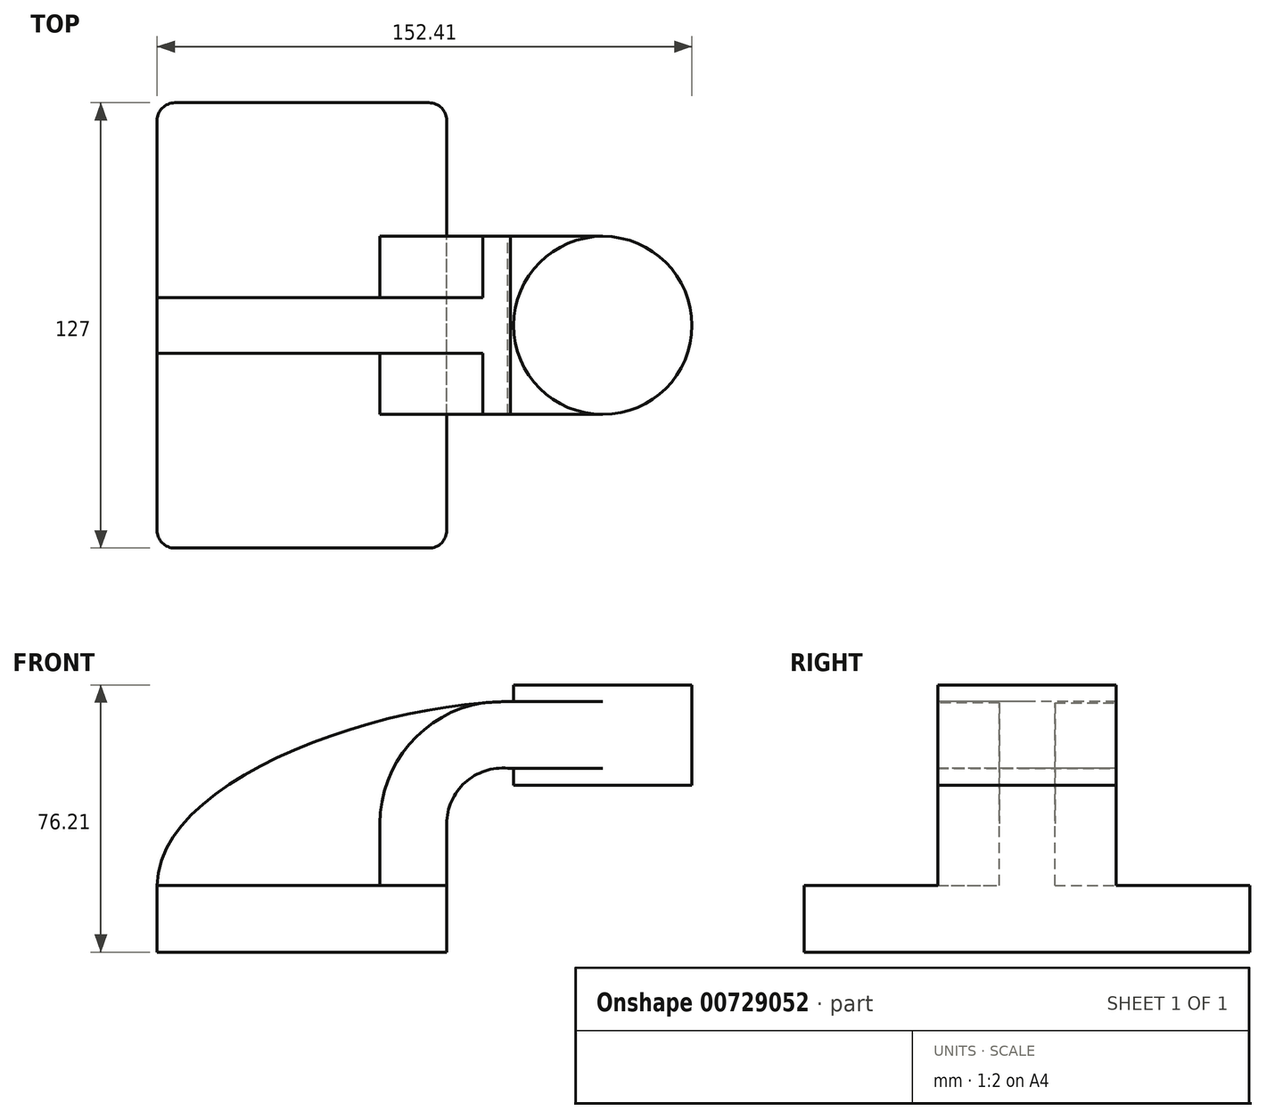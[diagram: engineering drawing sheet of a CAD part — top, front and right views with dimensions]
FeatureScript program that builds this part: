
annotation { "Feature Type Name" : "Feature", "Feature Type Description" : "" }
export const myFeature = defineFeature(function(context is Context, id is Id, definition is map)
    precondition{}
    {
        {
            var Q0;
            Q0=qCreatedBy(makeId("Front.planeOp"),FACE);
            var sketch = newSketch(context, id + "F0", { "sketchPlane" : qUnion([Q0])});
            skLineSegment(sketch, "E0.bottom", {"start": v(41.28, -9.52) * mm, "end": v(-41.28, -9.53) * mm});
            skLineSegment(sketch, "E0.top", {"start": v(41.28, 9.53) * mm, "end": v(-41.28, 9.53) * mm});
            skLineSegment(sketch, "E0.left", {"start": v(41.28, -9.52) * mm, "end": v(41.28, 9.53) * mm});
            skLineSegment(sketch, "E0.right", {"start": v(-41.28, -9.52) * mm, "end": v(-41.28, 9.53) * mm});
            skPoint(sketch, "E0.middle", {"position": v(0, 0) * mm});
            skLineSegment(sketch, "E1.bottom", {"start": v(111.12, 38.1) * mm, "end": v(60.32, 38.1) * mm});
            skLineSegment(sketch, "E1.top", {"start": v(111.12, 66.68) * mm, "end": v(60.32, 66.68) * mm});
            skLineSegment(sketch, "E1.left", {"start": v(111.12, 38.1) * mm, "end": v(111.12, 66.68) * mm});
            skLineSegment(sketch, "E1.right", {"start": v(60.32, 38.1) * mm, "end": v(60.32, 66.67) * mm});
            skPoint(sketch, "E1.middle", {"position": v(85.72, 52.39) * mm});
            skLineSegment(sketch, "E2", {"start": v(41.28, 9.53) * mm, "end": v(41.28, 27.07) * mm});
            skArc(sketch, "E3", {"start": v(41.27, 27.07) * mm, "mid": v(46.47, 38.82) * mm, "end": v(58.66, 42.88) * mm});
            skLineSegment(sketch, "E4", {"start": v(58.66, 42.88) * mm, "end": v(85.9, 42.88) * mm});
            skLineSegment(sketch, "E5.0", {"start": v(59.39, 61.93) * mm, "end": v(85.9, 61.93) * mm});
            skArc(sketch, "E5.1", {"start": v(22.23, 27.07) * mm, "mid": v(33.26, 52.55) * mm, "end": v(59.39, 61.93) * mm});
            skLineSegment(sketch, "E5.2", {"start": v(22.22, 9.53) * mm, "end": v(22.22, 27.07) * mm});
            skLineSegment(sketch, "E6", {"start": v(85.72, 38.1) * mm, "end": v(85.72, 66.68) * mm});
            skFitSpline(sketch, "E7", {"points": [v(-41.28, 9.52) * mm, v(59.39, 61.93) * mm], "startDerivative": vector(0.2, 88.51) * mm, "endDerivative": vector(118.13, 1.81) * mm});
            skSolve(sketch);
        }
        {
            var Q0;
            Q0=makeQuery(id+"F0.imprint","IMPRINT",FACE,{"disambiguationData":[TD([[makeQuery(id+"F0.imprint","IMPRINT",EDGE,{"derivedFrom":sQuery(id+"F0.wireOp",EDGE,"E0.bottom")}),-1.0]])]});
            extrude(context, id + "F1", {"entities" : qUnion([Q0]), "endBound" : BoundingType.SYMMETRIC, "depth" : 127 * mm, "offsetDistance" : 25.4 * mm});
        }
        {
            var Q0;
            {var subQ1=sQuery(id+"F0.wireOp",EDGE,"E2");Q0=makeQuery(id+"F0.imprint","IMPRINT",FACE,{"disambiguationData":[TD([[makeQuery(id+"F0.imprint","IMPRINT",EDGE,{"derivedFrom":subQ1}),1.0]])]});}
            var Q1;
            {var subQ0=sQuery(id+"F0.wireOp",EDGE,"E4");var subQ1=sQuery(id+"F0.wireOp",EDGE,"E1.right");var subQ2=makeQuery(id+"F0.imprint","INTERSECT",VERTEX,{"derivedFrom":[subQ1,subQ0]});Q1=makeQuery(id+"F0.imprint","IMPRINT",FACE,{"disambiguationData":[TD([[makeQuery(id+"F0.imprint","IMPRINT",EDGE,{"disambiguationData":[TD([[subQ2,-1.0]])],"derivedFrom":subQ1}),-1.0]])]});}
            extrude(context, id + "F2", {"entities" : qUnion([Q0, Q1]), "operationType" : NewBodyOperationType.ADD, "endBound" : BoundingType.SYMMETRIC, "depth" : 50.8 * mm, "offsetDistance" : 25.4 * mm});
        }
        {
            var Q0;
            {var subQ3=sQuery(id+"F0.wireOp",EDGE,"E5.2");Q0=makeQuery(id+"F0.imprint","IMPRINT",FACE,{"disambiguationData":[TD([[makeQuery(id+"F0.imprint","IMPRINT",EDGE,{"derivedFrom":subQ3}),1.0]])]});}
            extrude(context, id + "F3", {"entities" : qUnion([Q0]), "operationType" : NewBodyOperationType.ADD, "endBound" : BoundingType.SYMMETRIC, "depth" : 15.88 * mm, "offsetDistance" : 25.4 * mm});
        }
        {
            var Q0;
            {var subQ0=sQuery(id+"F0.wireOp",EDGE,"E1.left");Q0=makeQuery(id+"F0.imprint","IMPRINT",FACE,{"disambiguationData":[TD([[makeQuery(id+"F0.imprint","IMPRINT",EDGE,{"derivedFrom":subQ0}),1.0]])]});}
            var Q1;
            Q1=sQuery(id+"F0.wireOp",EDGE,"E6");
            revolve(context, id + "F4", {"operationType" : NewBodyOperationType.ADD, "surfaceOperationType" : NewSurfaceOperationType.NEW, "entities" : qUnion([Q0]), "axis" : qUnion([Q1]), "revolveType" : RevolveType.FULL});
        }
        {
            var Q0;
            Q0=makeQuery(id+"F1.opExtrude","CAP_EDGE",EDGE,{"disambiguationData":[OSD([sQuery(id+"F0.wireOp",EDGE,"E0.left")])],"isStart":false});
            var Q1;
            Q1=makeQuery(id+"F1.opExtrude","CAP_EDGE",EDGE,{"disambiguationData":[OSD([sQuery(id+"F0.wireOp",EDGE,"E0.left")])],"isStart":true});
            var Q2;
            Q2=makeQuery(id+"F1.opExtrude","CAP_EDGE",EDGE,{"disambiguationData":[OSD([sQuery(id+"F0.wireOp",EDGE,"E0.right")])],"isStart":true});
            var Q3;
            Q3=makeQuery(id+"F1.opExtrude","CAP_EDGE",EDGE,{"disambiguationData":[OSD([sQuery(id+"F0.wireOp",EDGE,"E0.right")])],"isStart":false});
            fillet(context, id + "F5", {"entities" : qUnion([Q0, Q1, Q2, Q3]), "radius" : 5.08 * mm, "tangentPropagation" : true, "allowEdgeOverflow" : false});
        }
    });
